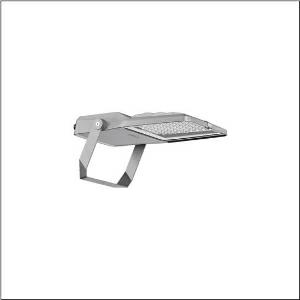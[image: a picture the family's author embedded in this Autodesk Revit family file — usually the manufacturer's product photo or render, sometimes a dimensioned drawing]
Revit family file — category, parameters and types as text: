
# Revit family: floodlight_fl_21_mini___rs12_5xa7772b2b1a_a572
name_source: partatom
category: Lighting Fixtures
units: mm (PartAtom-declared; Revit-internal decimal feet)

## family parameters
Cut with Voids When Loaded = No
Host = Face
Light Source = No
Part Type = Normal
Room Calculation Point = No
Round Connector Dimension = Use Diameter
Shared = No

## types (1)
- --- (1 x LED, 6300 lm, 45.5 W, 3000K)
    Apparent Load = 46 VA
    CIE Flux Codes = 79 92 99 100 100
    Color Rendering = 70
    Color Temperature = 3000K
    Default Elevation = 1800 mm
    Description = Floodlight FL 21 mini, floodlight, primary light control with lens, of PMMA, primary optical cover: protective disc, of toughened safety glass, transparent, light distribution: RS12, light emission: direct distribution, installation type: surface-mounted, LED, High Power LED, rated luminous flux: 6.300lm, luminous efficacy: 138lm/W, light colour: 730, colour temperature: 3000K, control gear: ECG iQ, control: Street-Remote, Auto-Match, Temp-Guard, Night-Set, Smart-Wire, Desk-Remote (wireless, voltage-free reading and setting of iQ features in the workshop via application-optimized NFC function/RFID function), optimised constant luminous flux control (CLO 2.0), with terminal, 6-pole, mains connection: 220..240V, AC, 50/60Hz, start of lifetime: 46W, end of lifetime: 48W, reduction: 22W, luminaire housing, of diecast aluminium, powder-coated, Siteco® metallic grey (DB 702S), corrosivity category C5 according to DIN EN ISO 12944, mounting bracket, of steel, galvanised, powder-coated, Siteco® metallic grey (DB 702S), protection rating (complete): IP66, insulation class (complete): insulation class II (safety insulation), certification: CE, ENEC, VDE, protection symbol: D, impact resistance: IK08, permissible operating ambient temperature: -40..+40°C, permissible operating ambient temperature for outdoor applications: -40..+50°C, standard: DIN EN 12944, packaging unit: 1 piece

Light Distribution: RS12
    Height = 70 mm
    Lamp = 1 x LED
    Lamp Light Flux = 6300 lm
    Lamp Power = 45.5 W
    Lamp count = 1
    Length = 485 mm
    Luminous efficacy = 138 lm/W
    Manufacturer = Siteco
    ModVariant = No
    Model = 5XA7772B2B1A
    Number of Poles = 1
    OnlyDefault = Yes
    Power Factor = 1
    Product Name = Floodlight FL 21 mini | RS12
    Product group = floodlight | pylon top
    ProductGroupID = 6101
    Protection Class = Protection class II
    Protection Degree = IP 66
    RLX_Detail_Level = 1
    RlxData = <blob elided: 90665 chars, md5=cc1a38b5>
    Socket = socket
    Standby Power = 0 W
    System Light Flux = 6300 lm
    System Power = 46 W
    Type Comments = factory setting: luminous flux: 100 % | dim-lin: 254 | 463 mA
    Type Image = l_1006845.jpg
    URL = http://relux.com
    VarID = @adj_078955
    Voltage = 0 V
    Weight = 0.00 kg
    Width = 337 mm

## geometry (parser evidence)
native form markers: Blend x4, Sweep x15
no freeform markers — native parametric forms only
